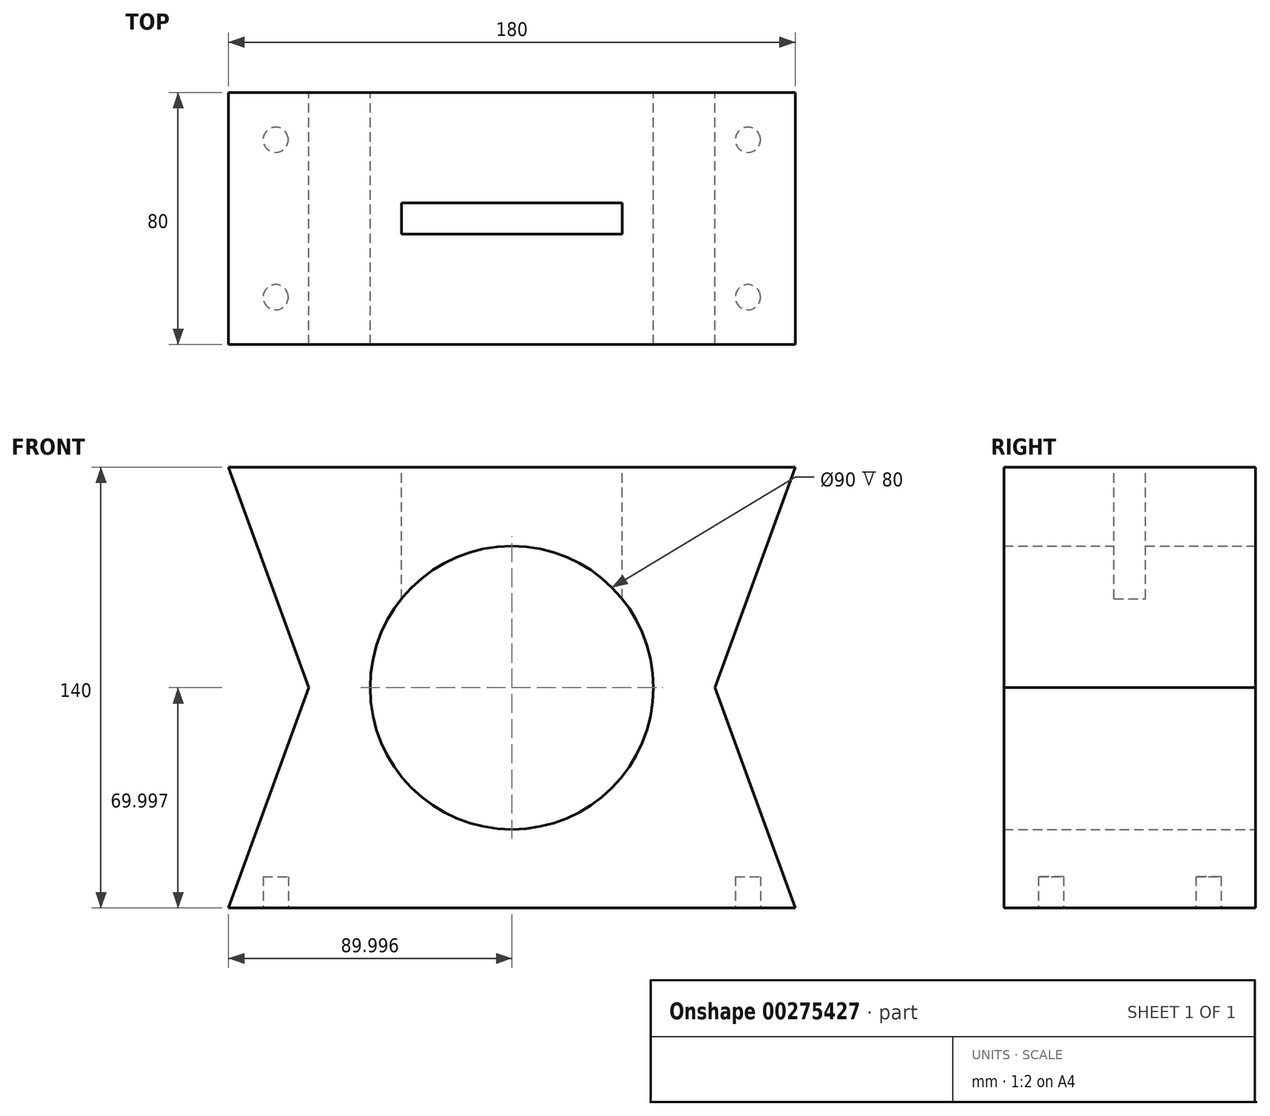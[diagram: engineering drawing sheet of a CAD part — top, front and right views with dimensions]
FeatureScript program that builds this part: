
annotation { "Feature Type Name" : "Feature", "Feature Type Description" : "" }
export const myFeature = defineFeature(function(context is Context, id is Id, definition is map)
    precondition{}
    {
        {
            var Q0;
            Q0=qCreatedBy(makeId("Front.planeOp"),FACE);
            var sketch = newSketch(context, id + "F0", { "sketchPlane" : qUnion([Q0])});
            skLineSegment(sketch, "E0.bottom", {"start": v(-93.08, 36.9) * mm, "end": v(86.92, 36.9) * mm});
            skLineSegment(sketch, "E0.top", {"start": v(-93.08, -103.1) * mm, "end": v(86.92, -103.1) * mm});
            skLineSegment(sketch, "E1", {"start": v(-93.08, 36.9) * mm, "end": v(-67.6, -33.1) * mm});
            skLineSegment(sketch, "E2", {"start": v(-67.6, -33.1) * mm, "end": v(-93.08, -103.1) * mm});
            skLineSegment(sketch, "E3", {"start": v(86.92, 36.9) * mm, "end": v(61.44, -33.1) * mm});
            skLineSegment(sketch, "E4", {"start": v(61.44, -33.1) * mm, "end": v(86.92, -103.1) * mm});
            skCircle(sketch, "E5", {"center": v(-3.08, -33.1) * mm, "radius": 45 * mm});
            skSolve(sketch);
        }
        {
            var Q0;
            Q0 = qSketchRegion(id + "F0", true);
            extrude(context, id + "F1", {"entities" : qUnion([Q0]), "depth" : 80 * mm, "offsetDistance" : 25 * mm});
        }
        {
            var Q0;
            Q0=makeQuery(id+"F1.opExtrude","SWEPT_FACE",FACE,{"disambiguationData":[OSD([sQuery(id+"F0.wireOp",EDGE,"E0.top")])]});
            var sketch = newSketch(context, id + "F2", { "sketchPlane" : qUnion([Q0])});
            skCircle(sketch, "E6", {"center": v(-78.08, 65) * mm, "radius": 4 * mm});
            skCircle(sketch, "E7", {"center": v(-78.08, 15) * mm, "radius": 4 * mm});
            skCircle(sketch, "E8", {"center": v(71.92, 15) * mm, "radius": 4 * mm});
            skCircle(sketch, "E9", {"center": v(71.92, 65) * mm, "radius": 4 * mm});
            skSolve(sketch);
        }
        {
            var Q0;
            Q0 = qSketchRegion(id + "F2", true);
            extrude(context, id + "F3", {"entities" : qUnion([Q0]), "operationType" : NewBodyOperationType.REMOVE, "oppositeDirection" : true, "depth" : 10 * mm});
        }
        {
            var Q0;
            Q0=makeQuery(id+"F1.opExtrude","SWEPT_FACE",FACE,{"disambiguationData":[OSD([sQuery(id+"F0.wireOp",EDGE,"E0.bottom")])]});
            var sketch = newSketch(context, id + "F4", { "sketchPlane" : qUnion([Q0])});
            skLineSegment(sketch, "E10.bottom", {"start": v(-38.08, -35) * mm, "end": v(31.92, -35) * mm});
            skLineSegment(sketch, "E10.top", {"start": v(-38.08, -45) * mm, "end": v(31.92, -45) * mm});
            skLineSegment(sketch, "E10.left", {"start": v(-38.08, -35) * mm, "end": v(-38.08, -45) * mm});
            skLineSegment(sketch, "E10.right", {"start": v(31.92, -35) * mm, "end": v(31.92, -45) * mm});
            skSolve(sketch);
        }
        {
            var Q0;
            Q0 = qSketchRegion(id + "F4", true);
            extrude(context, id + "F5", {"entities" : qUnion([Q0]), "operationType" : NewBodyOperationType.REMOVE, "oppositeDirection" : true, "depth" : 53.5 * mm});
        }
    });
